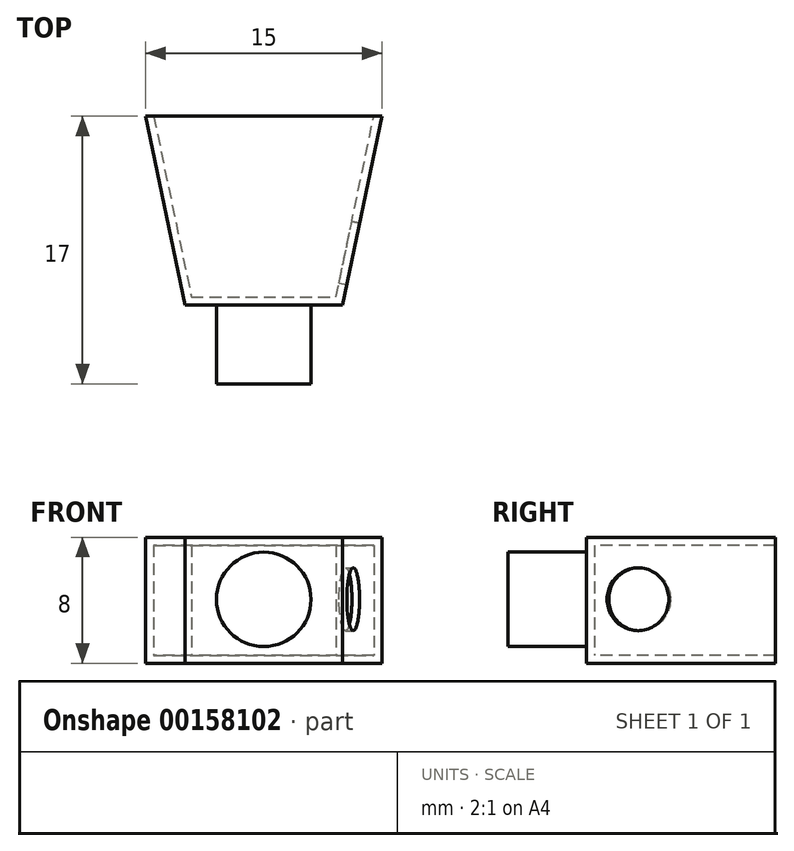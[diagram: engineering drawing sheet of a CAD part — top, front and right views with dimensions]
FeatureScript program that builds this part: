
annotation { "Feature Type Name" : "Feature", "Feature Type Description" : "" }
export const myFeature = defineFeature(function(context is Context, id is Id, definition is map)
    precondition{}
    {
        {
            var Q0;
            Q0=qCreatedBy(makeId("Top.planeOp"),FACE);
            var sketch = newSketch(context, id + "F0", { "sketchPlane" : qUnion([Q0])});
            skLineSegment(sketch, "E0", {"start": v(-5, -12) * mm, "end": v(5, -12) * mm});
            skLineSegment(sketch, "E1", {"start": v(5, -12) * mm, "end": v(7.5, 0) * mm});
            skLineSegment(sketch, "E2", {"start": v(7.5, 0) * mm, "end": v(-7.5, 0) * mm});
            skLineSegment(sketch, "E3", {"start": v(-7.5, 0) * mm, "end": v(-5, -12) * mm});
            skSolve(sketch);
        }
        {
            var Q0;
            Q0=makeQuery(id+"F0.imprint","IMPRINT",FACE,{"disambiguationData":[TD([[makeQuery(id+"F0.imprint","IMPRINT",EDGE,{"derivedFrom":sQuery(id+"F0.wireOp",EDGE,"E0")}),1.0]])]});
            extrude(context, id + "F1", {"entities" : qUnion([Q0]), "depth" : 8 * mm});
        }
        {
            var Q0;
            Q0=makeQuery(id+"F1.opExtrude","SWEPT_FACE",FACE,{"disambiguationData":[OSD([sQuery(id+"F0.wireOp",EDGE,"E2")])]});
            shell(context, id + "F2", {"entities" : qUnion([Q0]), "thickness" : 0.5 * mm});
        }
        {
            var Q0;
            Q0=makeQuery(id+"F1.opExtrude","SWEPT_FACE",FACE,{"disambiguationData":[OSD([sQuery(id+"F0.wireOp",EDGE,"E0")])]});
            var sketch = newSketch(context, id + "F3", { "sketchPlane" : qUnion([Q0])});
            skCircle(sketch, "E4", {"center": v(0, 4.06) * mm, "radius": 3 * mm});
            skSolve(sketch);
        }
        {
            var Q0;
            Q0=makeQuery(id+"F3.imprint","IMPRINT",FACE,{"disambiguationData":[TD([[makeQuery(id+"F3.imprint","IMPRINT",EDGE,{"derivedFrom":sQuery(id+"F3.wireOp",EDGE,"E4")}),1.0]])]});
            extrude(context, id + "F4", {"entities" : qUnion([Q0]), "operationType" : NewBodyOperationType.ADD, "depth" : 5 * mm});
        }
        {
            var Q0;
            Q0=makeQuery(id+"F1.opExtrude","SWEPT_FACE",FACE,{"disambiguationData":[OSD([sQuery(id+"F0.wireOp",EDGE,"E1")])]});
            var sketch = newSketch(context, id + "F5", { "sketchPlane" : qUnion([Q0])});
            skCircle(sketch, "E5", {"center": v(-7.4, 4.07) * mm, "radius": 2 * mm});
            skSolve(sketch);
        }
        {
            var Q0;
            Q0=makeQuery(id+"F5.imprint","IMPRINT",FACE,{"disambiguationData":[TD([[makeQuery(id+"F5.imprint","IMPRINT",EDGE,{"derivedFrom":sQuery(id+"F5.wireOp",EDGE,"E5")}),1.0]])]});
            extrude(context, id + "F6", {"entities" : qUnion([Q0]), "operationType" : NewBodyOperationType.REMOVE, "oppositeDirection" : true, "depth" : 5 * mm});
        }
    });
